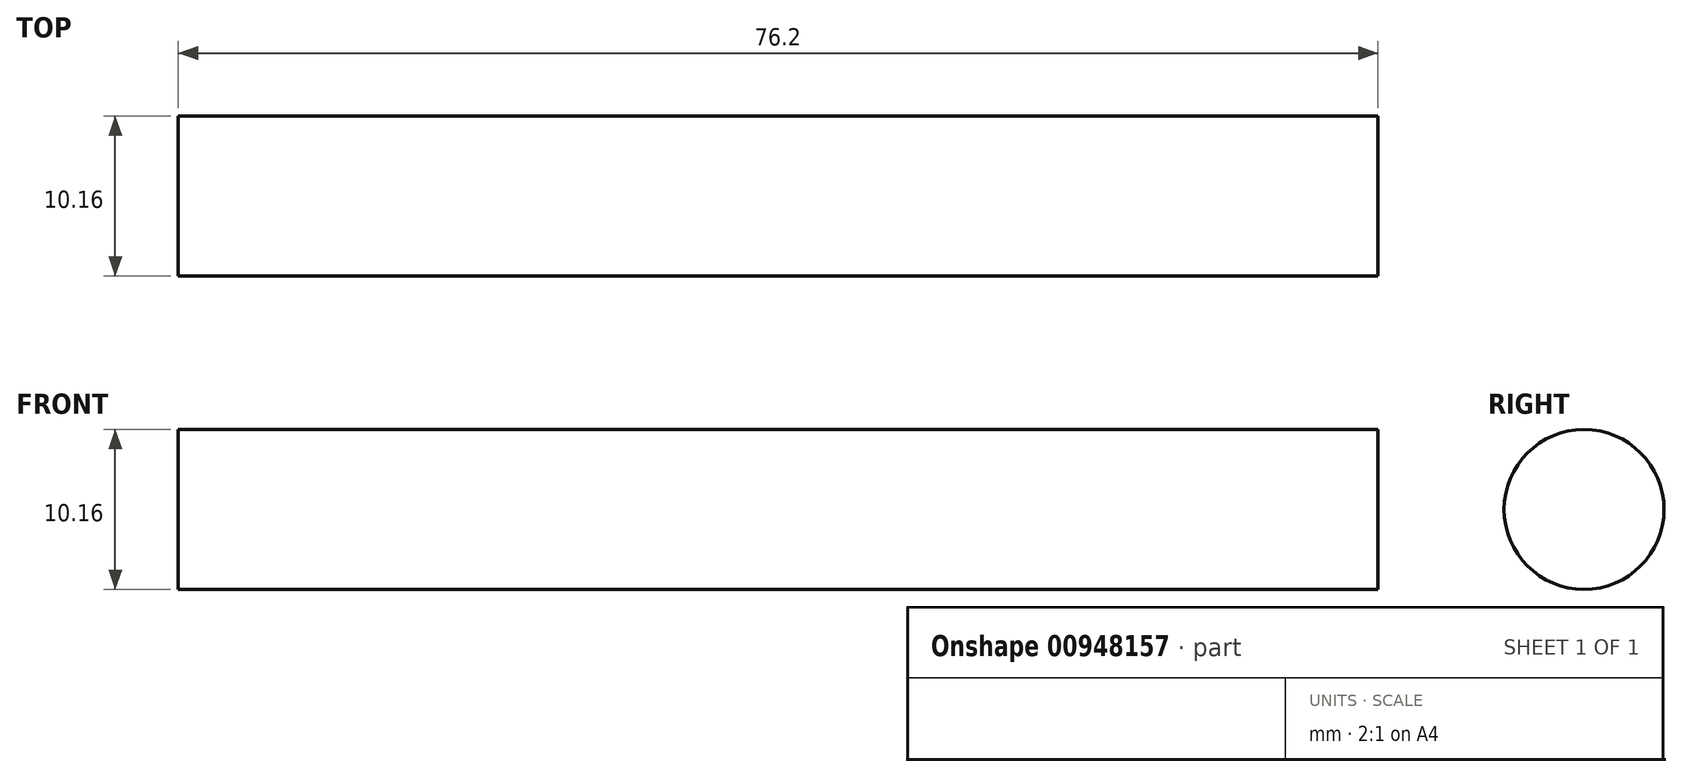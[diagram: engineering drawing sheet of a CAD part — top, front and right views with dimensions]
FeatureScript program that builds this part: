
annotation { "Feature Type Name" : "Feature", "Feature Type Description" : "" }
export const myFeature = defineFeature(function(context is Context, id is Id, definition is map)
    precondition{}
    {
        {
            var Q0;
            Q0=qCreatedBy(makeId("Right.planeOp"),FACE);
            var sketch = newSketch(context, id + "F0", { "sketchPlane" : qUnion([Q0])});
            skCircle(sketch, "E0", {"center": v(32.48, 29.67) * mm, "radius": 5.08 * mm});
            skSolve(sketch);
        }
        {
            var Q0;
            Q0=makeQuery(id+"F0.imprint","IMPRINT",FACE,{"disambiguationData":[TD([[makeQuery(id+"F0.imprint","IMPRINT",EDGE,{"derivedFrom":sQuery(id+"F0.wireOp",EDGE,"E0")}),1.0]])]});
            extrude(context, id + "F1", {"entities" : qUnion([Q0]), "depth" : 76.2 * mm, "offsetDistance" : 25.4 * mm});
        }
    });
